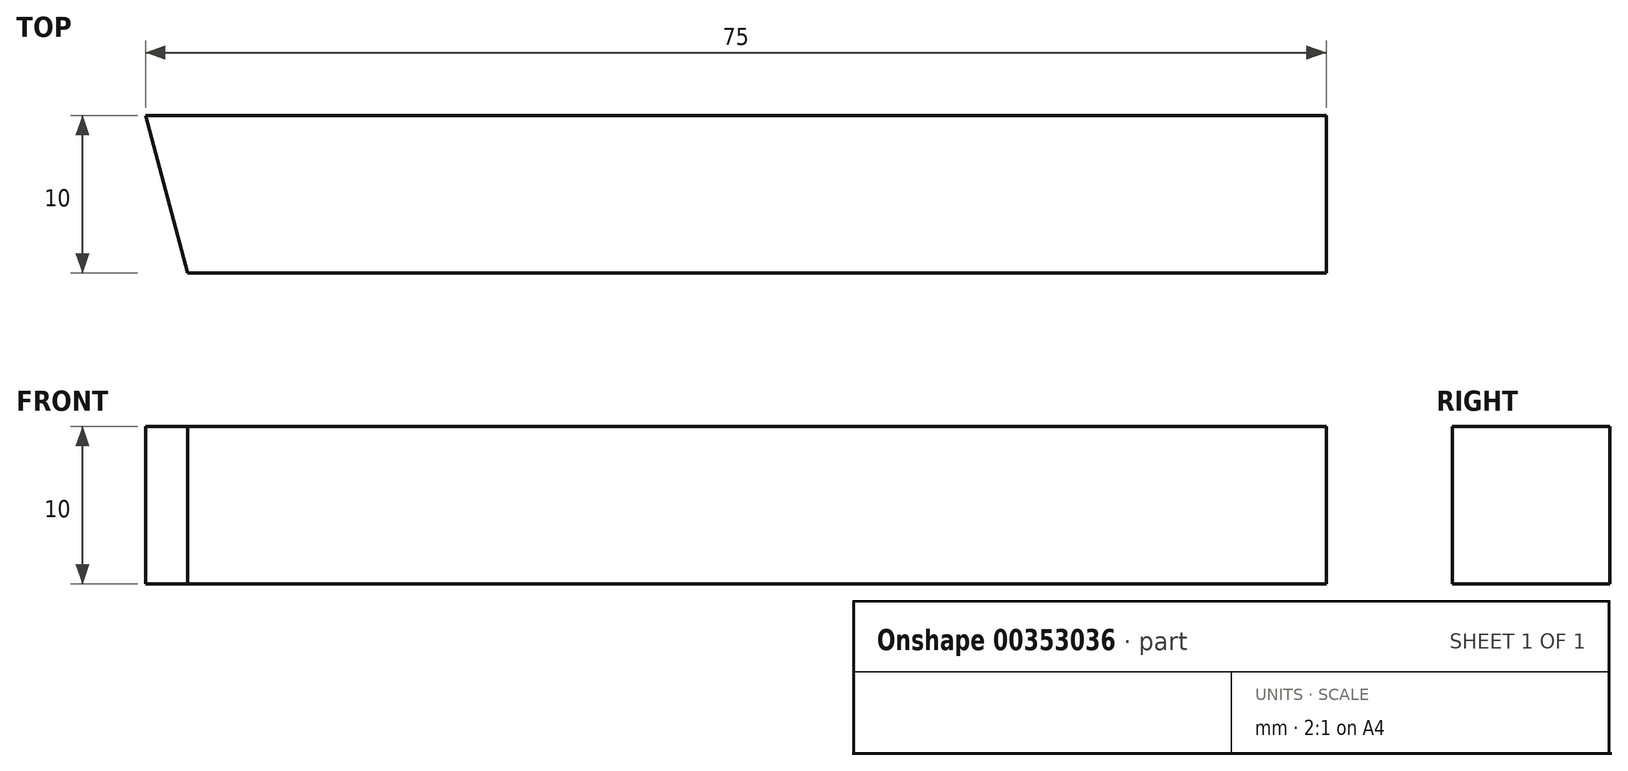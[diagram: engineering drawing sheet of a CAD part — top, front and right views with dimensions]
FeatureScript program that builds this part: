
annotation { "Feature Type Name" : "Feature", "Feature Type Description" : "" }
export const myFeature = defineFeature(function(context is Context, id is Id, definition is map)
    precondition{}
    {
        {
            var Q0;
            Q0=qCreatedBy(makeId("Top.planeOp"),FACE);
            var sketch = newSketch(context, id + "F0", { "sketchPlane" : qUnion([Q0])});
            skLineSegment(sketch, "E0.bottom", {"start": v(0, 0) * mm, "end": v(75, 0) * mm});
            skLineSegment(sketch, "E0.top", {"start": v(0, 10) * mm, "end": v(75, 10) * mm});
            skLineSegment(sketch, "E0.left", {"start": v(0, 0) * mm, "end": v(0, 10) * mm});
            skLineSegment(sketch, "E0.right", {"start": v(75, 0) * mm, "end": v(75, 10) * mm});
            skLineSegment(sketch, "E1.bottom", {"start": v(37.24, -7.37) * mm, "end": v(36.2, -7.37) * mm});
            skLineSegment(sketch, "E1.top", {"start": v(37.24, -5.56) * mm, "end": v(36.2, -5.56) * mm});
            skLineSegment(sketch, "E1.left", {"start": v(37.24, -7.37) * mm, "end": v(37.24, -5.56) * mm});
            skLineSegment(sketch, "E1.right", {"start": v(36.2, -7.37) * mm, "end": v(36.2, -5.56) * mm});
            skLineSegment(sketch, "E2", {"start": v(0, 10) * mm, "end": v(16.93, -53.19) * mm});
            skSolve(sketch);
        }
        {
            var Q0;
            {var subQ4=sQuery(id+"F0.wireOp",EDGE,"E0.top");Q0=makeQuery(id+"F0.imprint","IMPRINT",FACE,{"disambiguationData":[TD([[makeQuery(id+"F0.imprint","IMPRINT",EDGE,{"derivedFrom":subQ4}),-1.0]])]});}
            extrude(context, id + "F1", {"entities" : qUnion([Q0]), "depth" : 10 * mm});
        }
    });
